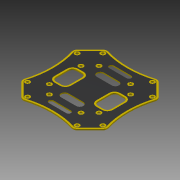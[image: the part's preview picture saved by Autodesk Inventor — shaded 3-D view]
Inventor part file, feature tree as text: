
AUTODESK INVENTOR PART (.ipt)
format: ipt  version: 2015 (Build 190159000, 159)  size: 504,832 bytes
history: native  units: in
note: dims shown in document units (in); Inventor stores cm internally (conversion verified against a paired STEP export)
features: mirror x1, other x1, imported_body x1
ambient origin geometry x8: Origin, YZ Plane, XZ Plane, XY Plane, X Axis, Y Axis, Z Axis, Center Point
bodies: Body1 (feature_tree)
feature tree (3):
  mirror  "Mirror1"
  other  "F450 Top Plate1"
  imported_body  "Base1"
